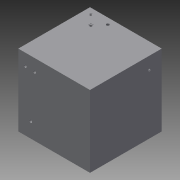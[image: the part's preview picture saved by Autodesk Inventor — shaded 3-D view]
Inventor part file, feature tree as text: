
AUTODESK INVENTOR PART (.ipt)
format: ipt  version: 2014 (Build 180170000, 170)  size: 348,160 bytes
history: native  units: mm
features: other x54, sketch x15, extrude x1
ambient origin geometry x8: Origin, YZ Plane, XZ Plane, XY Plane, X Axis, Y Axis, Z Axis, Center Point
bodies: 实体1 (feature_tree)
feature tree (70):
  extrude  "拉伸1"  TaperAngle=0.0deg  [1 undecoded]
  other  "UCS1"
  other  "UCS2"
  other  "UCS3"
  other  "UCS4"
  other  "UCS5"
  other  "UCS6"
  other  "iFeature7:2"
  other  "iFeature7:3"
  other  "iFeature7:4"
  other  "iFeature7:5"
  other  "iFeature7:6"
  other  "iFeature7:7"
  sketch  "草图1"  dims[d0=400.0mm d1=0.0mm]
  other  "UCS1: YZ 平面"
  other  "UCS1: XZ 平面"
  other  "UCS1: XY 平面"
  other  "UCS1: X 轴"
  other  "UCS1: Y 轴"
  other  "UCS1: Z 轴"
  other  "UCS1: 原点"
  other  "UCS2: YZ 平面"
  other  "UCS2: XZ 平面"
  other  "UCS2: XY 平面"
  other  "UCS2: X 轴"
  other  "UCS2: Y 轴"
  other  "UCS2: Z 轴"
  other  "UCS2: 原点"
  other  "UCS3: YZ 平面"
  other  "UCS3: XZ 平面"
  other  "UCS3: XY 平面"
  other  "UCS3: X 轴"
  other  "UCS3: Y 轴"
  other  "UCS3: Z 轴"
  other  "UCS3: 原点"
  other  "UCS4: YZ 平面"
  other  "UCS4: XZ 平面"
  other  "UCS4: XY 平面"
  other  "UCS4: X 轴"
  other  "UCS4: Y 轴"
  other  "UCS4: Z 轴"
  other  "UCS4: 原点"
  other  "UCS5: YZ 平面"
  other  "UCS5: XZ 平面"
  other  "UCS5: XY 平面"
  other  "UCS5: X 轴"
  other  "UCS5: Y 轴"
  other  "UCS5: Z 轴"
  other  "UCS5: 原点"
  other  "UCS6: YZ 平面"
  other  "UCS6: XZ 平面"
  other  "UCS6: XY 平面"
  other  "UCS6: X 轴"
  other  "UCS6: Y 轴"
  other  "UCS6: Z 轴"
  other  "UCS6: 原点"
  sketch  "草图2"  dims[d2=0.0mm d3=0.0mm d4=0.0mm d5=0.0mm d6=0.0mm d7=0.0mm]
  sketch  "草图3"  dims[d8=0.0mm d9=0.0mm d10=0.0mm d11=0.0mm d12=0.0mm d13=0.0mm]
  sketch  "草图4"  dims[d14=0.0mm d15=0.0mm d16=0.0mm d17=0.0mm d18=0.0mm d19=0.0mm]
  sketch  "草图5"  dims[d20=0.0mm d21=0.0mm d22=0.0mm d23=0.0mm d24=0.0mm d25=0.0mm]
  sketch  "草图6"  dims[d26=0.0mm d27=0.0mm d28=0.0mm d29=0.0mm d30=0.0mm d31=0.0mm]
  sketch  "草图8"  dims[d32=0.0mm d33=0.0mm d34=0.0mm d35=0.0mm d36=0.0mm d37=0.0mm d38=0.0mm]
  sketch  "草图9"  dims[d42=0.0mm]
  sketch  "草图10"  dims[d46=0.0mm]
  sketch  "草图11"  dims[d50=0.0mm]
  sketch  "草图12"  dims[d54=0.0mm]
  sketch  "草图13"  dims[d58=0.0mm]
  sketch  "草图14"  dims[d62=0.0mm]
  sketch  "草图15"  dims[d66=0.0mm]
  sketch  "草图16"  dims[d76=0.0mm]
note: 1 required parameter value undecoded (feature->parameter linkage not recoverable at this tier; creation-order binding heuristic only, values carry confidence <= 0.55)
